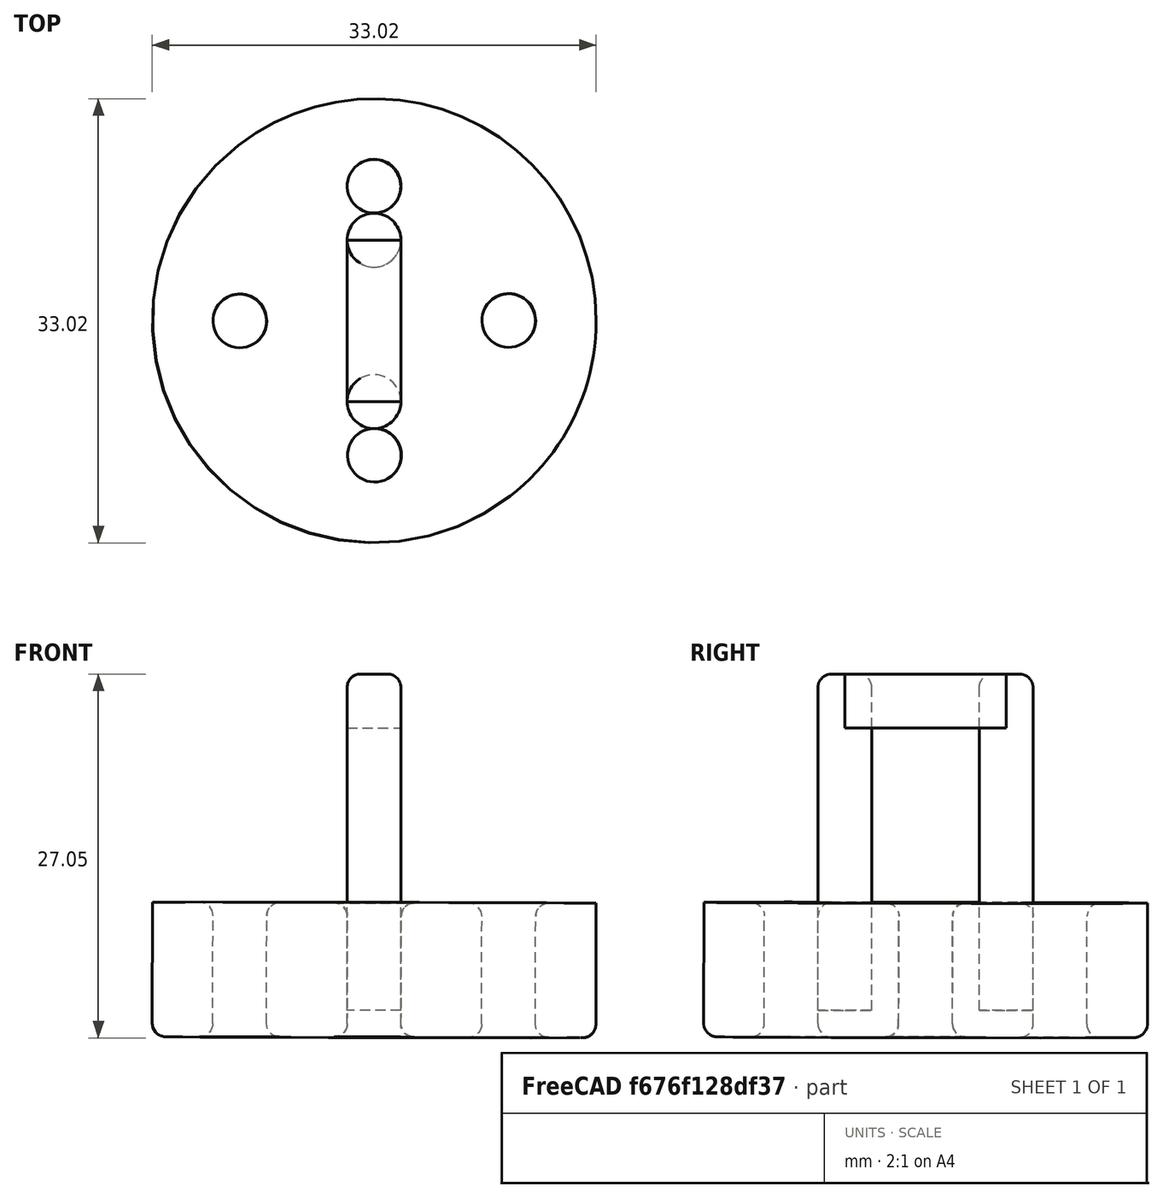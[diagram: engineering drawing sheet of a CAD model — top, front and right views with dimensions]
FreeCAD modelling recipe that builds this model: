
FCSTD DOCUMENT  (FreeCAD 0.15R4671 (Git))
Label: projeteurV3
License: All rights reserved
LicenseURL: http://en.wikipedia.org/wiki/All_rights_reserved
objects: Part::Cylinder×7, Part::Cut×4, Part::Fillet×4, Part::Box×1, App::DocumentObjectGroup×1
note: 16 computed .brp shape members not serialized (recipe doc carries the construction recipe); baked Part::Feature solids carry a one-line shape summary decoded from their .brp

FEATURE [Part::Cylinder] Cylinder  label="base"
  Angle = 360
  Height = 10
  Radius = 16.5
FEATURE [Part::Box] Box  label="Cube"
  Height = 4
  Length = 4
  Placement = pos=(-2,-6,16) rot=(0,0,1;0rad)
  Width = 12
FEATURE [Part::Cylinder] Cylinder001  label="Cylindre001"
  Angle = 360
  Height = 10
  Placement = pos=(0,10,0) rot=(0,0,1;0rad)
  Radius = 2
FEATURE [Part::Cylinder] Cylinder002  label="Cylindre002"
  Angle = 360
  Height = 10
  Placement = pos=(0,-10,0) rot=(0,0,1;0rad)
  Radius = 2
FEATURE [Part::Cylinder] Cylinder004  label="Cylindre004"
  Angle = 360
  Height = 10
  Placement = pos=(-10,0,0) rot=(0,0,1;0rad)
  Radius = 2
FEATURE [Part::Cylinder] Cylinder005  label="Cylindre005"
  Angle = 360
  Height = 10
  Placement = pos=(10,0,0) rot=(0,0,1;0rad)
  Radius = 2
FEATURE [Part::Cut] Cut
  Base = -> Cylinder
  Tool = -> Cylinder005
FEATURE [Part::Cut] Cut001
  Base = -> Cut
  Tool = -> Cylinder001
FEATURE [Part::Cut] Cut002
  Base = -> Cut001
  Tool = -> Cylinder002
FEATURE [Part::Cut] Cut003
  Base = -> Cut002
  Placement = pos=(0,0,-7) rot=(-0.556894,0.719072,0.415698;0.003347rad)
  Tool = -> Cylinder004
FEATURE [Part::Cylinder] Cylinder006  label="Cylindre"
  Angle = 360
  Height = 25
  Placement = pos=(0,6,-5) rot=(0,0,1;0rad)
  Radius = 2
FEATURE [Part::Cylinder] Cylinder007  label="Cylindre006"
  Angle = 360
  Height = 25
  Placement = pos=(0,-6,-5) rot=(0,0,1;0rad)
  Radius = 2
FEATURE [Part::Fillet] Fillet
  Base = -> Box
  Edges = 2 edges r=1: [Edge2,Edge6]
FEATURE [Part::Fillet] Fillet001
  Base = -> Cylinder007
  Edges = 1 edges r=1: [Edge1]
FEATURE [Part::Fillet] Fillet002
  Base = -> Cylinder006
  Edges = 1 edges r=1: [Edge1]
FEATURE [App::DocumentObjectGroup] Groupe  label="poignée"
  Group = -> [Cylinder007,Cylinder006,Box,Fillet,Fillet001,Fillet002]
FEATURE [Part::Fillet] Fillet003  label="base001"
  Base = -> Cut003
  Edges = 9 edges r=1: [Edge3,Edge4,Edge5,Edge6,Edge7,Edge8,Edge9,Edge10,Edge11]
